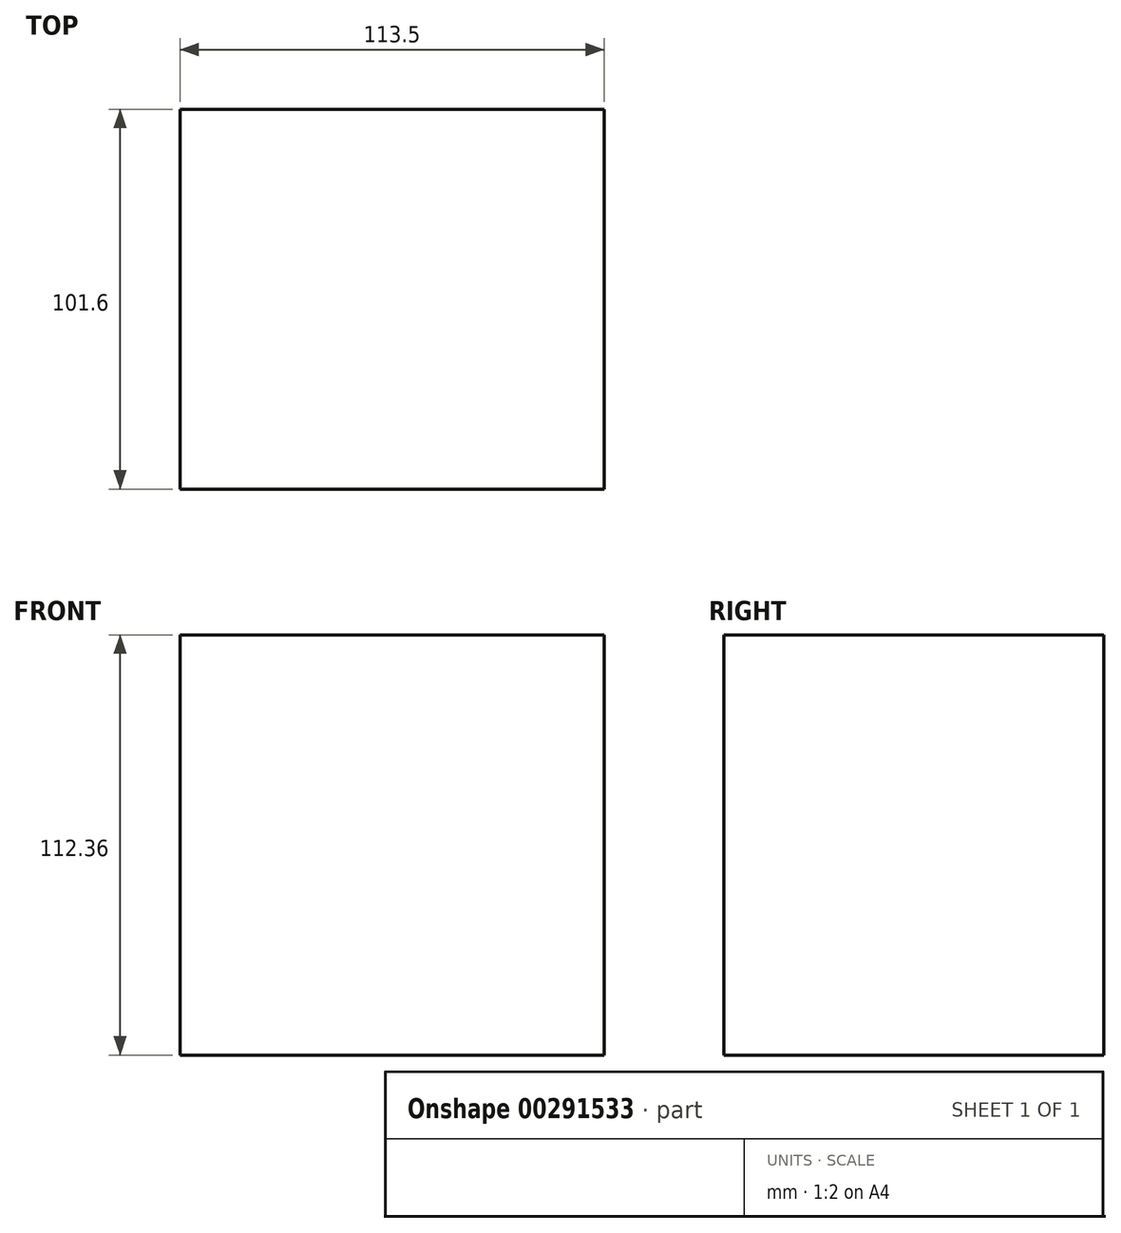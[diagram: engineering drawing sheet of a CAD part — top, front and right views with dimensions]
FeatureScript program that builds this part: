
annotation { "Feature Type Name" : "Feature", "Feature Type Description" : "" }
export const myFeature = defineFeature(function(context is Context, id is Id, definition is map)
    precondition{}
    {
        {
            var Q0;
            Q0=qCreatedBy(makeId("Front.planeOp"),FACE);
            var sketch = newSketch(context, id + "F0", { "sketchPlane" : qUnion([Q0])});
            skLineSegment(sketch, "E0", {"start": v(61.33, 0) * mm, "end": v(61.33, -61.48) * mm});
            skLineSegment(sketch, "E1", {"start": v(61.33, -61.48) * mm, "end": v(-52.17, -61.48) * mm});
            skLineSegment(sketch, "E2", {"start": v(-52.17, -61.48) * mm, "end": v(-52.17, 50.88) * mm});
            skLineSegment(sketch, "E3", {"start": v(-52.17, 50.88) * mm, "end": v(61.33, 50.88) * mm});
            skLineSegment(sketch, "E4", {"start": v(61.33, 50.88) * mm, "end": v(61.33, 0) * mm});
            skSolve(sketch);
        }
        {
            var Q0;
            Q0 = qSketchRegion(id + "F0", true);
            extrude(context, id + "F1", {"entities" : qUnion([Q0]), "depth" : 50.8 * mm});
        }
        {
            var Q0;
            Q0=makeQuery(id+"F1.opExtrude","CAP_FACE",FACE,{"disambiguationData":[OSD([sQuery(id+"F0.wireOp",EDGE,"E0"),sQuery(id+"F0.wireOp",EDGE,"E1"),sQuery(id+"F0.wireOp",EDGE,"E2"),sQuery(id+"F0.wireOp",EDGE,"E3"),sQuery(id+"F0.wireOp",EDGE,"E4")])],"isStart":true});
            var sketch = newSketch(context, id + "F2", { "sketchPlane" : qUnion([Q0])});
            skLineSegment(sketch, "E5", {"start": v(-61.33, -61.48) * mm, "end": v(-61.33, 50.88) * mm});
            skLineSegment(sketch, "E6", {"start": v(-61.33, 50.88) * mm, "end": v(52.17, 50.88) * mm});
            skLineSegment(sketch, "E7", {"start": v(52.17, 50.88) * mm, "end": v(52.17, -61.48) * mm});
            skLineSegment(sketch, "E8", {"start": v(52.17, -61.48) * mm, "end": v(-61.33, -61.48) * mm});
            skSolve(sketch);
        }
        {
            var Q0;
            Q0=makeQuery(id+"F2.imprint","IMPRINT",FACE,{"disambiguationData":[TD([[makeQuery(id+"F2.imprint","IMPRINT",EDGE,{"derivedFrom":sQuery(id+"F2.wireOp",EDGE,"E5")}),1.0]])]});
            extrude(context, id + "F3", {"entities" : qUnion([Q0]), "operationType" : NewBodyOperationType.ADD, "depth" : 50.8 * mm});
        }
    });
